# Revit family: PRD_FrankeWS_DrnkngFntnPckgs_DrinkingBubbler_AQRM304
name_source: partatom
category: Plumbing Fixtures
revit_build: Autodesk Revit 2018 (Build: 20190510_1515(x64)
units: mm (PartAtom-declared; Revit-internal decimal feet)

## family parameters
Cut with Voids When Loaded = No
Host = Face
OmniClass Number = 23.45.55.14
OmniClass Title = Single Faucets
Part Type = Normal
Room Calculation Point = No
Round Connector Dimension = Use Diameter
Shared = No

## types (1)
- AQRM304
    AssetType = Fixed
    BIMObjectName = PRD_AR_DrinkingFountainPackages_DrinkingBubbler_AQRM304
    Category = Pr_40_20_87_24, Drinking fountains
    Default Elevation = 0 mm  [stored 0 ft]
    Description = Drinking bubbler DN 15, with push cap and anti-twist protection, polished chromium-plated brass. Connection G 3/8 B.
    DiameterNominal = 1/2"
    DurationUnit = year
    FaucetFunction = COLD
    FaucetOperation = SELFCLOSING
    FaucetType = PILLAR
    Flow = 0.1 L/s
    FormUnit = Counter top mounting
    GrossWeight = 0.58 kg
    IfcExportAs = IfcValveType
    IfcExportType = FAUCET
    Manufacturer = KWC Group AG
    ManufacturerName = KWC Group AG
    ManufacturerURL = www.kwc.com
    Model = AQRM304
    ModelNumber = 2000101118
    ModelReference = AQRM304
    NBSDescription = Drinking fountain packages
    NBSReference = 45-35-70/400
    Name = Drinking bubbler AQRM304
    NetWeight = 0.55 kg
    NominalDiameter = DN 15 (3-8 inch)
    NominalHeight = 0 mm  [stored 0 ft]
    NominalLength = 0 mm  [stored 0 ft]
    NominalWidth = 0 mm  [stored 0 ft]
    ProductInformation = https://pim.kwc.com
    TapMaterial = PRD_AR_ChromatedBrass_HighPolished
    URL = www.kwc.com
    Uniclass2015Code = Pr_40_20_87_24
    Uniclass2015Title = Drinking fountains
    Uniclass2015Version = Products v1.7
    Version = 1
    WarrantyDurationUnit = year

note: [stored X ft] marks values corroborated as IEEE doubles in the binary element streams (Revit-internal decimal feet)

## geometry (parser evidence)
native form markers: Sweep x2
no freeform markers — native parametric forms only
